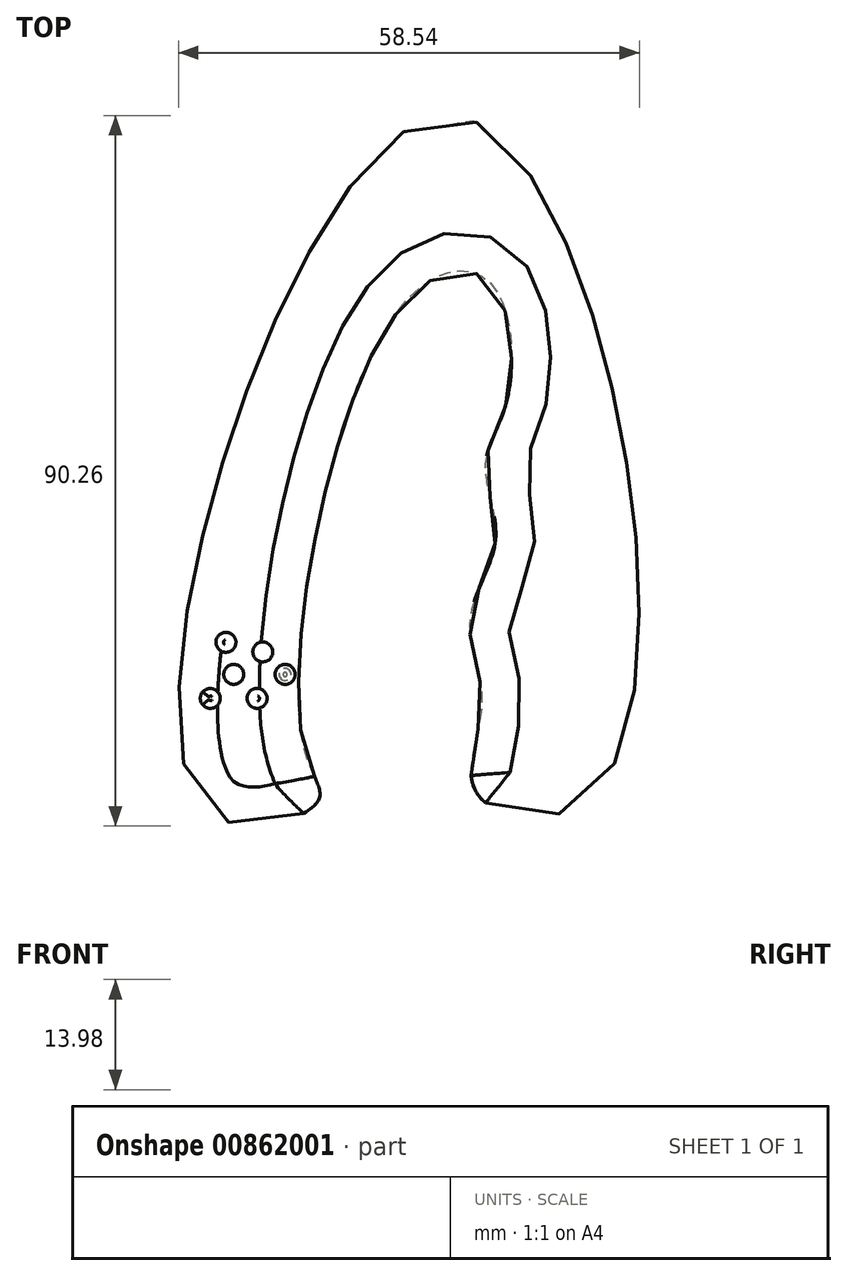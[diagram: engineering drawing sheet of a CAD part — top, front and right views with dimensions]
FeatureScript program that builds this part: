
annotation { "Feature Type Name" : "Feature", "Feature Type Description" : "" }
export const myFeature = defineFeature(function(context is Context, id is Id, definition is map)
    precondition{}
    {
        {
            var Q0;
            Q0=qCreatedBy(makeId("Top.planeOp"),FACE);
            var sketch = newSketch(context, id + "F0", { "sketchPlane" : qUnion([Q0])});
            skFitSpline(sketch, "E0", {"points": [v(-27.05, -33.55) * mm, v(-42.3, -32.58) * mm, v(-10.26, 53.88) * mm, v(10.27, -29.5) * mm, v(-6.47, -32.4) * mm, v(-6, -20.88) * mm, v(-7.48, -10.08) * mm, v(-4.23, 0) * mm, v(-5.55, 9.4) * mm, v(-2.78, 17.72) * mm, v(-5.02, 32.72) * mm, v(-16.37, 29.38) * mm, v(-28.67, -26.01) * mm, v(-27.05, -33.55) * mm]});
            skCircle(sketch, "E1", {"center": v(-40.47, -20.15) * mm, "radius": 1.27 * mm});
            skCircle(sketch, "E2", {"center": v(-37.5, -17.11) * mm, "radius": 1.27 * mm});
            skCircle(sketch, "E3", {"center": v(-33.8, -14.25) * mm, "radius": 1.27 * mm});
            skCircle(sketch, "E4", {"center": v(-30.97, -17.11) * mm, "radius": 1.27 * mm});
            skCircle(sketch, "E5", {"center": v(-34.52, -20.15) * mm, "radius": 1.27 * mm});
            skCircle(sketch, "E6", {"center": v(-38.48, -13.03) * mm, "radius": 1.27 * mm});
            skSolve(sketch);
        }
        {
            var Q0;
            Q0=makeQuery(id+"F0.imprint","IMPRINT",FACE,{"disambiguationData":[TD([[makeQuery(id+"F0.imprint","IMPRINT",EDGE,{"derivedFrom":sQuery(id+"F0.wireOp",EDGE,"E0")}),-1.0]])]});
            extrude(context, id + "F1", {"entities" : qUnion([Q0]), "endBound" : BoundingType.SYMMETRIC, "depth" : 12.7 * mm, "offsetDistance" : 25.4 * mm});
        }
        {
            var Q0;
            Q0=makeQuery(id+"F1.opExtrude","CAP_EDGE",EDGE,{"disambiguationData":[OSD([sQuery(id+"F0.wireOp",EDGE,"E0")])],"isStart":false});
            var Q1;
            Q1=makeQuery(id+"F1.opExtrude","CAP_EDGE",EDGE,{"disambiguationData":[OSD([sQuery(id+"F0.wireOp",EDGE,"E0")])],"isStart":true});
            fillet(context, id + "F2", {"entities" : qUnion([Q0, Q1]), "radius" : 4.95 * mm, "tangentPropagation" : true, "allowEdgeOverflow" : false});
        }
        {
            var Q0;
            Q0=makeQuery(id+"F0.imprint","IMPRINT",FACE,{"disambiguationData":[TD([[makeQuery(id+"F0.imprint","IMPRINT",EDGE,{"derivedFrom":sQuery(id+"F0.wireOp",EDGE,"E6")}),1.0]])]});
            var Q1;
            Q1=makeQuery(id+"F0.imprint","IMPRINT",FACE,{"disambiguationData":[TD([[makeQuery(id+"F0.imprint","IMPRINT",EDGE,{"derivedFrom":sQuery(id+"F0.wireOp",EDGE,"E3")}),1.0]])]});
            var Q2;
            Q2=makeQuery(id+"F0.imprint","IMPRINT",FACE,{"disambiguationData":[TD([[makeQuery(id+"F0.imprint","IMPRINT",EDGE,{"derivedFrom":sQuery(id+"F0.wireOp",EDGE,"E2")}),1.0]])]});
            var Q3;
            Q3=makeQuery(id+"F0.imprint","IMPRINT",FACE,{"disambiguationData":[TD([[makeQuery(id+"F0.imprint","IMPRINT",EDGE,{"derivedFrom":sQuery(id+"F0.wireOp",EDGE,"E4")}),1.0]])]});
            var Q4;
            Q4=makeQuery(id+"F0.imprint","IMPRINT",FACE,{"disambiguationData":[TD([[makeQuery(id+"F0.imprint","IMPRINT",EDGE,{"derivedFrom":sQuery(id+"F0.wireOp",EDGE,"E5")}),1.0]])]});
            var Q5;
            Q5=makeQuery(id+"F0.imprint","IMPRINT",FACE,{"disambiguationData":[TD([[makeQuery(id+"F0.imprint","IMPRINT",EDGE,{"derivedFrom":sQuery(id+"F0.wireOp",EDGE,"E1")}),1.0]])]});
            extrude(context, id + "F3", {"entities" : qUnion([Q0, Q1, Q2, Q3, Q4, Q5]), "operationType" : NewBodyOperationType.ADD, "endBound" : BoundingType.SYMMETRIC, "depth" : 13.97 * mm, "offsetDistance" : 25.4 * mm});
        }
        {
            var Q0;
            Q0=makeQuery(id+"F3.opExtrude","CAP_EDGE",EDGE,{"disambiguationData":[OSD([sQuery(id+"F0.wireOp",EDGE,"E6")])],"isStart":false});
            var Q1;
            Q1=makeQuery(id+"F3.opExtrude","CAP_EDGE",EDGE,{"disambiguationData":[OSD([sQuery(id+"F0.wireOp",EDGE,"E3")])],"isStart":false});
            var Q2;
            Q2=makeQuery(id+"F3.opExtrude","CAP_EDGE",EDGE,{"disambiguationData":[OSD([sQuery(id+"F0.wireOp",EDGE,"E2")])],"isStart":false});
            var Q3;
            Q3=makeQuery(id+"F3.opExtrude","CAP_EDGE",EDGE,{"disambiguationData":[OSD([sQuery(id+"F0.wireOp",EDGE,"E4")])],"isStart":false});
            var Q4;
            Q4=makeQuery(id+"F3.opExtrude","CAP_EDGE",EDGE,{"disambiguationData":[OSD([sQuery(id+"F0.wireOp",EDGE,"E5")])],"isStart":false});
            var Q5;
            Q5=makeQuery(id+"F3.opExtrude","CAP_EDGE",EDGE,{"disambiguationData":[OSD([sQuery(id+"F0.wireOp",EDGE,"E1")])],"isStart":false});
            var Q6;
            Q6=makeQuery(id+"F3.opExtrude","CAP_EDGE",EDGE,{"disambiguationData":[OSD([sQuery(id+"F0.wireOp",EDGE,"E1")])],"isStart":true});
            var Q7;
            Q7=makeQuery(id+"F3.opExtrude","CAP_EDGE",EDGE,{"disambiguationData":[OSD([sQuery(id+"F0.wireOp",EDGE,"E2")])],"isStart":true});
            var Q8;
            Q8=makeQuery(id+"F3.opExtrude","CAP_EDGE",EDGE,{"disambiguationData":[OSD([sQuery(id+"F0.wireOp",EDGE,"E6")])],"isStart":true});
            var Q9;
            Q9=makeQuery(id+"F3.opExtrude","CAP_EDGE",EDGE,{"disambiguationData":[OSD([sQuery(id+"F0.wireOp",EDGE,"E3")])],"isStart":true});
            var Q10;
            Q10=makeQuery(id+"F3.opExtrude","CAP_EDGE",EDGE,{"disambiguationData":[OSD([sQuery(id+"F0.wireOp",EDGE,"E5")])],"isStart":true});
            var Q11;
            Q11=makeQuery(id+"F3.opExtrude","CAP_EDGE",EDGE,{"disambiguationData":[OSD([sQuery(id+"F0.wireOp",EDGE,"E4")])],"isStart":true});
            fillet(context, id + "F4", {"entities" : qUnion([Q0, Q1, Q2, Q3, Q4, Q5, Q6, Q7, Q8, Q9, Q10, Q11]), "radius" : 1.02 * mm, "tangentPropagation" : true, "allowEdgeOverflow" : false});
        }
    });
